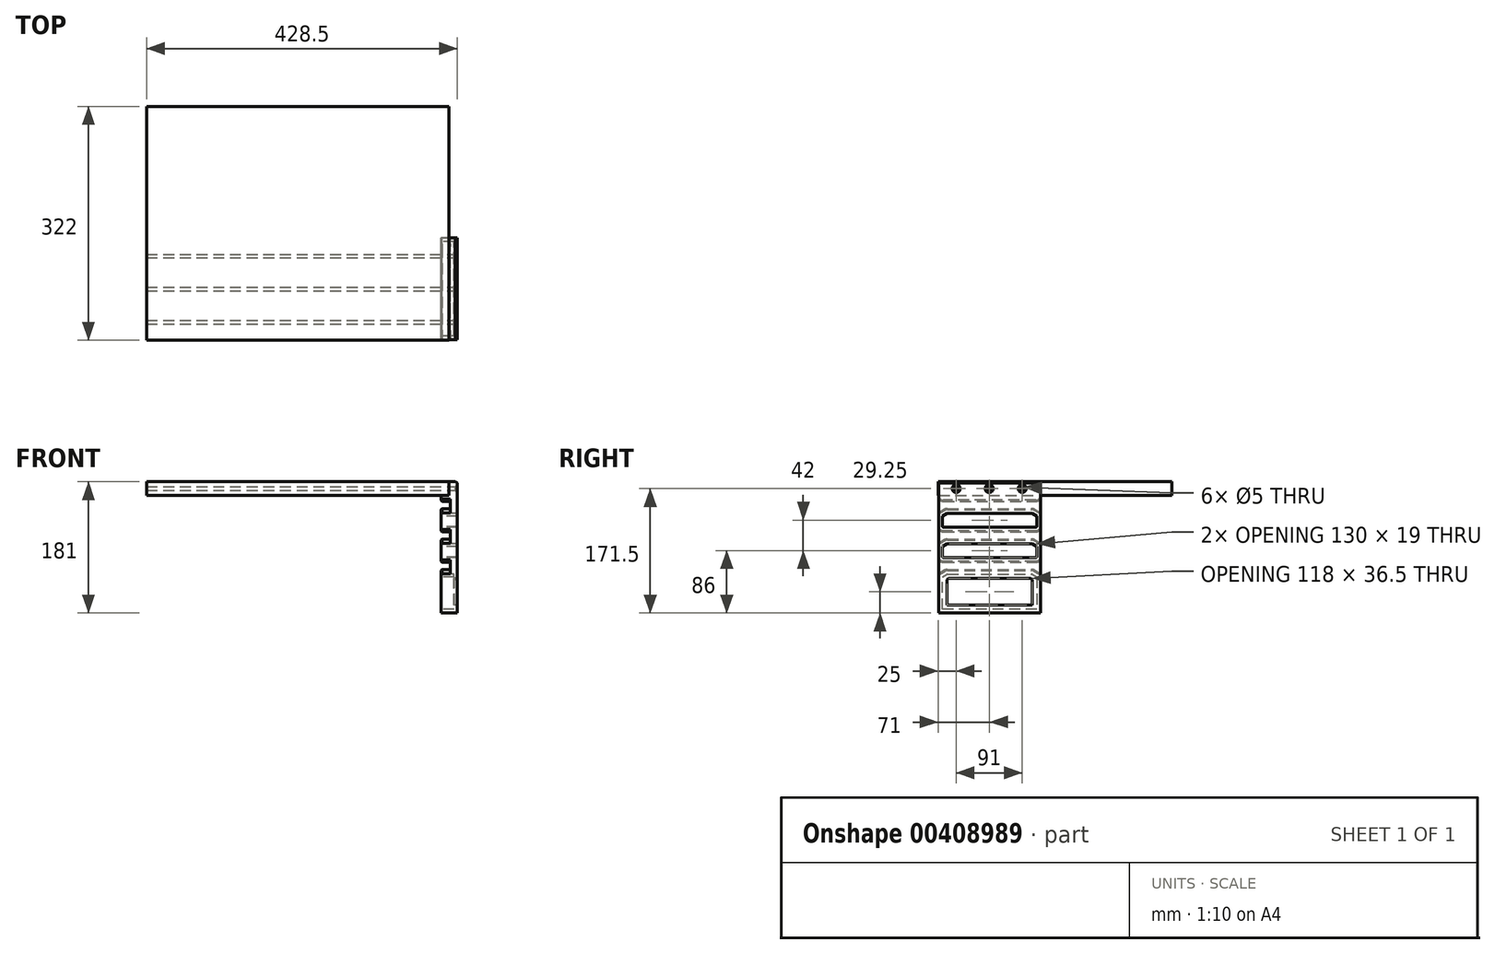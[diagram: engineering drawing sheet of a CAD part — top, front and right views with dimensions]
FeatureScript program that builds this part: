
annotation { "Feature Type Name" : "Feature", "Feature Type Description" : "" }
export const myFeature = defineFeature(function(context is Context, id is Id, definition is map)
    precondition{}
    {
        {
            var Q0;
            Q0=qCreatedBy(makeId("Front.planeOp"),FACE);
            var sketch = newSketch(context, id + "F0", { "sketchPlane" : qUnion([Q0])});
            skLineSegment(sketch, "E0.bottom", {"start": v(0, 0) * mm, "end": v(208.5, 0) * mm});
            skLineSegment(sketch, "E0.top", {"start": v(0, 19) * mm, "end": v(208.5, 19) * mm});
            skLineSegment(sketch, "E0.left", {"start": v(0, 0) * mm, "end": v(0, 19) * mm});
            skLineSegment(sketch, "E0.right", {"start": v(208.5, 0) * mm, "end": v(208.5, 19) * mm});
            skSolve(sketch);
        }
        {
            var Q0;
            Q0=makeQuery(id+"F0.imprint","IMPRINT",FACE,{"disambiguationData":[TD([[makeQuery(id+"F0.imprint","IMPRINT",EDGE,{"derivedFrom":sQuery(id+"F0.wireOp",EDGE,"E0.bottom")}),1.0]])]});
            extrude(context, id + "F1", {"entities" : qUnion([Q0]), "depth" : 161 * mm});
        }
        {
            var Q0;
            Q0=makeQuery(id+"F1.opExtrude","SWEPT_BODY",BODY,{"disambiguationData":[OSD([sQuery(id+"F0.wireOp",EDGE,"E0.bottom"),sQuery(id+"F0.wireOp",EDGE,"E0.top"),sQuery(id+"F0.wireOp",EDGE,"E0.left"),sQuery(id+"F0.wireOp",EDGE,"E0.right")])]});
            var Q1;
            Q1=makeQuery(id+"F1.opExtrude","CAP_FACE",FACE,{"disambiguationData":[OSD([sQuery(id+"F0.wireOp",EDGE,"E0.bottom"),sQuery(id+"F0.wireOp",EDGE,"E0.top"),sQuery(id+"F0.wireOp",EDGE,"E0.left"),sQuery(id+"F0.wireOp",EDGE,"E0.right")])],"isStart":true});
            mirror(context, id + "F2", {"operationType" : NewBodyOperationType.ADD, "entities" : qUnion([Q0]), "mirrorPlane" : qUnion([Q1])});
        }
        {
            var Q0;
            Q0=makeQuery(id+"F1.opExtrude","SWEPT_BODY",BODY,{"disambiguationData":[OSD([sQuery(id+"F0.wireOp",EDGE,"E0.bottom"),sQuery(id+"F0.wireOp",EDGE,"E0.top"),sQuery(id+"F0.wireOp",EDGE,"E0.left"),sQuery(id+"F0.wireOp",EDGE,"E0.right")])]});
            var Q1;
            {var subQ0=makeQuery(id+"F1.opExtrude","SWEPT_FACE",FACE,{"disambiguationData":[OSD([sQuery(id+"F0.wireOp",EDGE,"E0.left")])]});Q1=makeQuery(id+"F2.boolean.opBoolean","MERGE",FACE,{"derivedFrom":[subQ0,makeQuery(id+"F2.opPattern","COPY",FACE,{"derivedFrom":subQ0,"instanceName":"1"})]});}
            mirror(context, id + "F3", {"operationType" : NewBodyOperationType.ADD, "entities" : qUnion([Q0]), "mirrorPlane" : qUnion([Q1])});
        }
        {
            var Q0;
            Q0=qCreatedBy(makeId("Front.planeOp"),FACE);
            var sketch = newSketch(context, id + "F4", { "sketchPlane" : qUnion([Q0])});
            skLineSegment(sketch, "E1", {"start": v(208.5, 19) * mm, "end": v(208.5, 0) * mm});
            skLineSegment(sketch, "E2", {"start": v(208.5, 0) * mm, "end": v(197.5, 0) * mm});
            skLineSegment(sketch, "E3", {"start": v(197.5, 0) * mm, "end": v(197.5, -8) * mm});
            skLineSegment(sketch, "E4", {"start": v(197.5, -8) * mm, "end": v(210, -8) * mm});
            skLineSegment(sketch, "E5", {"start": v(210, -8) * mm, "end": v(210, -18) * mm});
            skLineSegment(sketch, "E6", {"start": v(210, -18) * mm, "end": v(197.5, -18) * mm});
            skLineSegment(sketch, "E7", {"start": v(197.5, -18) * mm, "end": v(197.5, -50) * mm});
            skLineSegment(sketch, "E8", {"start": v(197.5, -50) * mm, "end": v(210, -50) * mm});
            skLineSegment(sketch, "E9", {"start": v(210, -50) * mm, "end": v(210, -60) * mm});
            skLineSegment(sketch, "E10", {"start": v(210, -60) * mm, "end": v(197.5, -60) * mm});
            skLineSegment(sketch, "E11", {"start": v(197.5, -60) * mm, "end": v(197.5, -92) * mm});
            skLineSegment(sketch, "E12", {"start": v(197.5, -162) * mm, "end": v(220, -162) * mm});
            skLineSegment(sketch, "E13", {"start": v(220, -162) * mm, "end": v(220, 19) * mm});
            skLineSegment(sketch, "E14", {"start": v(220, 19) * mm, "end": v(208.5, 19) * mm});
            skLineSegment(sketch, "E15.0", {"start": v(208.5, 0) * mm, "end": v(208.5, 19) * mm});
            skLineSegment(sketch, "E16", {"start": v(197.5, -92) * mm, "end": v(210, -92) * mm});
            skLineSegment(sketch, "E17", {"start": v(210, -92) * mm, "end": v(210, -102) * mm});
            skLineSegment(sketch, "E18", {"start": v(210, -102) * mm, "end": v(197.5, -102) * mm});
            skLineSegment(sketch, "E19.trimOffspring", {"start": v(197.5, -102) * mm, "end": v(197.5, -162) * mm});
            skSolve(sketch);
        }
        {
            var Q0;
            Q0=makeQuery(id+"F4.imprint","IMPRINT",FACE,{"disambiguationData":[TD([[makeQuery(id+"F4.imprint","IMPRINT",EDGE,{"derivedFrom":sQuery(id+"F4.wireOp",EDGE,"E2")}),1.0]])]});
            extrude(context, id + "F5", {"entities" : qUnion([Q0]), "depth" : 160 * mm, "hasSecondDirection" : true, "secondDirectionOppositeDirection" : false, "secondDirectionDepth" : 20 * mm});
        }
        {
            var Q0;
            Q0=makeQuery(id+"F5.opExtrude","CAP_EDGE",EDGE,{"disambiguationData":[OSD([sQuery(id+"F4.wireOp",EDGE,"E6")])],"isStart":false});
            var Q1;
            Q1=makeQuery(id+"F5.opExtrude","CAP_EDGE",EDGE,{"disambiguationData":[OSD([sQuery(id+"F4.wireOp",EDGE,"E10")])],"isStart":false});
            var Q2;
            Q2=makeQuery(id+"F5.opExtrude","CAP_EDGE",EDGE,{"disambiguationData":[OSD([sQuery(id+"F4.wireOp",EDGE,"E18")])],"isStart":false});
            chamfer(context, id + "F6", {"entities" : qUnion([Q0, Q1, Q2]), "chamferType" : ChamferType.OFFSET_ANGLE, "width" : 10 * mm, "oppositeDirection" : true, "angle" : 30 * degree, "tangentPropagation" : true});
        }
        {
            var Q0;
            Q0=makeQuery(id+"F5.opExtrude","CAP_EDGE",EDGE,{"disambiguationData":[OSD([sQuery(id+"F4.wireOp",EDGE,"E6")])],"isStart":true});
            var Q1;
            Q1=makeQuery(id+"F5.opExtrude","CAP_EDGE",EDGE,{"disambiguationData":[OSD([sQuery(id+"F4.wireOp",EDGE,"E10")])],"isStart":true});
            var Q2;
            Q2=makeQuery(id+"F5.opExtrude","CAP_EDGE",EDGE,{"disambiguationData":[OSD([sQuery(id+"F4.wireOp",EDGE,"E18")])],"isStart":true});
            chamfer(context, id + "F7", {"entities" : qUnion([Q0, Q1, Q2]), "chamferType" : ChamferType.OFFSET_ANGLE, "width" : 10 * mm, "oppositeDirection" : false, "angle" : 30 * degree, "tangentPropagation" : true});
        }
        {
            var Q0;
            Q0=makeQuery(id+"F5.opExtrude","CAP_EDGE",EDGE,{"disambiguationData":[OSD([sQuery(id+"F4.wireOp",EDGE,"E4")])],"isStart":true});
            var Q1;
            Q1=makeQuery(id+"F5.opExtrude","CAP_EDGE",EDGE,{"disambiguationData":[OSD([sQuery(id+"F4.wireOp",EDGE,"E8")])],"isStart":true});
            var Q2;
            Q2=makeQuery(id+"F5.opExtrude","CAP_EDGE",EDGE,{"disambiguationData":[OSD([sQuery(id+"F4.wireOp",EDGE,"E16")])],"isStart":true});
            var Q3;
            Q3=makeQuery(id+"F5.opExtrude","CAP_EDGE",EDGE,{"disambiguationData":[OSD([sQuery(id+"F4.wireOp",EDGE,"E16")])],"isStart":false});
            var Q4;
            Q4=makeQuery(id+"F5.opExtrude","CAP_EDGE",EDGE,{"disambiguationData":[OSD([sQuery(id+"F4.wireOp",EDGE,"E8")])],"isStart":false});
            var Q5;
            Q5=makeQuery(id+"F5.opExtrude","CAP_EDGE",EDGE,{"disambiguationData":[OSD([sQuery(id+"F4.wireOp",EDGE,"E4")])],"isStart":false});
            chamfer(context, id + "F8", {"entities" : qUnion([Q0, Q1, Q2, Q3, Q4, Q5]), "width" : 3 * mm, "tangentPropagation" : true});
        }
        {
            var Q0;
            Q0=makeQuery(id+"F5.opExtrude","SWEPT_EDGE",EDGE,{"disambiguationData":[OSD([sQuery(id+"F4.wireOp",EDGE,"E13"),sQuery(id+"F4.wireOp",EDGE,"E14")])]});
            chamfer(context, id + "F9", {"entities" : qUnion([Q0]), "chamferType" : ChamferType.OFFSET_ANGLE, "width" : 3 * mm, "oppositeDirection" : false, "angle" : 30 * degree, "tangentPropagation" : true});
        }
        {
            var Q0;
            {var subQ0=sQuery(id+"F4.wireOp",EDGE,"E18");Q0=makeQuery(id+"F7.opChamfer","BLEND_EDGE",EDGE,{"blendedFrom":[makeQuery(id+"F5.opExtrude","CAP_EDGE",EDGE,{"disambiguationData":[OSD([subQ0])],"isStart":true}),makeQuery(id+"F5.opExtrude","SWEPT_FACE",FACE,{"disambiguationData":[OSD([subQ0])]})],"blendedInto":[makeQuery(id+"F5.opExtrude","SWEPT_FACE",FACE,{"disambiguationData":[OSD([subQ0])]})]});}
            var Q1;
            {var subQ0=sQuery(id+"F4.wireOp",EDGE,"E18");Q1=makeQuery(id+"F6.opChamfer","BLEND_EDGE",EDGE,{"blendedFrom":[makeQuery(id+"F5.opExtrude","CAP_EDGE",EDGE,{"disambiguationData":[OSD([subQ0])],"isStart":false}),makeQuery(id+"F5.opExtrude","SWEPT_FACE",FACE,{"disambiguationData":[OSD([subQ0])]})],"blendedInto":[makeQuery(id+"F5.opExtrude","SWEPT_FACE",FACE,{"disambiguationData":[OSD([subQ0])]})]});}
            var Q2;
            {var subQ0=sQuery(id+"F4.wireOp",EDGE,"E10");Q2=makeQuery(id+"F6.opChamfer","BLEND_EDGE",EDGE,{"blendedFrom":[makeQuery(id+"F5.opExtrude","CAP_EDGE",EDGE,{"disambiguationData":[OSD([subQ0])],"isStart":false}),makeQuery(id+"F5.opExtrude","SWEPT_FACE",FACE,{"disambiguationData":[OSD([subQ0])]})],"blendedInto":[makeQuery(id+"F5.opExtrude","SWEPT_FACE",FACE,{"disambiguationData":[OSD([subQ0])]})]});}
            var Q3;
            {var subQ0=sQuery(id+"F4.wireOp",EDGE,"E6");Q3=makeQuery(id+"F6.opChamfer","BLEND_EDGE",EDGE,{"blendedFrom":[makeQuery(id+"F5.opExtrude","CAP_EDGE",EDGE,{"disambiguationData":[OSD([subQ0])],"isStart":false}),makeQuery(id+"F5.opExtrude","SWEPT_FACE",FACE,{"disambiguationData":[OSD([subQ0])]})],"blendedInto":[makeQuery(id+"F5.opExtrude","SWEPT_FACE",FACE,{"disambiguationData":[OSD([subQ0])]})]});}
            var Q4;
            {var subQ0=sQuery(id+"F4.wireOp",EDGE,"E10");Q4=makeQuery(id+"F7.opChamfer","BLEND_EDGE",EDGE,{"blendedFrom":[makeQuery(id+"F5.opExtrude","CAP_EDGE",EDGE,{"disambiguationData":[OSD([subQ0])],"isStart":true}),makeQuery(id+"F5.opExtrude","SWEPT_FACE",FACE,{"disambiguationData":[OSD([subQ0])]})],"blendedInto":[makeQuery(id+"F5.opExtrude","SWEPT_FACE",FACE,{"disambiguationData":[OSD([subQ0])]})]});}
            var Q5;
            {var subQ0=sQuery(id+"F4.wireOp",EDGE,"E6");Q5=makeQuery(id+"F7.opChamfer","BLEND_EDGE",EDGE,{"blendedFrom":[makeQuery(id+"F5.opExtrude","CAP_EDGE",EDGE,{"disambiguationData":[OSD([subQ0])],"isStart":true}),makeQuery(id+"F5.opExtrude","SWEPT_FACE",FACE,{"disambiguationData":[OSD([subQ0])]})],"blendedInto":[makeQuery(id+"F5.opExtrude","SWEPT_FACE",FACE,{"disambiguationData":[OSD([subQ0])]})]});}
            var Q6;
            {var subQ0=sQuery(id+"F4.wireOp",EDGE,"E4");Q6=makeQuery(id+"F8.opChamfer","BLEND_EDGE",EDGE,{"blendedFrom":[makeQuery(id+"F5.opExtrude","CAP_EDGE",EDGE,{"disambiguationData":[OSD([subQ0])],"isStart":true}),makeQuery(id+"F5.opExtrude","SWEPT_FACE",FACE,{"disambiguationData":[OSD([subQ0])]})],"blendedInto":[makeQuery(id+"F5.opExtrude","SWEPT_FACE",FACE,{"disambiguationData":[OSD([subQ0])]})]});}
            var Q7;
            {var subQ0=sQuery(id+"F4.wireOp",EDGE,"E4");Q7=makeQuery(id+"F8.opChamfer","BLEND_EDGE",EDGE,{"blendedFrom":[makeQuery(id+"F5.opExtrude","CAP_EDGE",EDGE,{"disambiguationData":[OSD([subQ0])],"isStart":false}),makeQuery(id+"F5.opExtrude","SWEPT_FACE",FACE,{"disambiguationData":[OSD([subQ0])]})],"blendedInto":[makeQuery(id+"F5.opExtrude","SWEPT_FACE",FACE,{"disambiguationData":[OSD([subQ0])]})]});}
            var Q8;
            {var subQ0=sQuery(id+"F4.wireOp",EDGE,"E8");Q8=makeQuery(id+"F8.opChamfer","BLEND_EDGE",EDGE,{"blendedFrom":[makeQuery(id+"F5.opExtrude","CAP_EDGE",EDGE,{"disambiguationData":[OSD([subQ0])],"isStart":true}),makeQuery(id+"F5.opExtrude","SWEPT_FACE",FACE,{"disambiguationData":[OSD([subQ0])]})],"blendedInto":[makeQuery(id+"F5.opExtrude","SWEPT_FACE",FACE,{"disambiguationData":[OSD([subQ0])]})]});}
            var Q9;
            {var subQ0=sQuery(id+"F4.wireOp",EDGE,"E16");Q9=makeQuery(id+"F8.opChamfer","BLEND_EDGE",EDGE,{"blendedFrom":[makeQuery(id+"F5.opExtrude","CAP_EDGE",EDGE,{"disambiguationData":[OSD([subQ0])],"isStart":true}),makeQuery(id+"F5.opExtrude","SWEPT_FACE",FACE,{"disambiguationData":[OSD([subQ0])]})],"blendedInto":[makeQuery(id+"F5.opExtrude","SWEPT_FACE",FACE,{"disambiguationData":[OSD([subQ0])]})]});}
            var Q10;
            {var subQ0=sQuery(id+"F4.wireOp",EDGE,"E16");Q10=makeQuery(id+"F8.opChamfer","BLEND_EDGE",EDGE,{"blendedFrom":[makeQuery(id+"F5.opExtrude","CAP_EDGE",EDGE,{"disambiguationData":[OSD([subQ0])],"isStart":false}),makeQuery(id+"F5.opExtrude","SWEPT_FACE",FACE,{"disambiguationData":[OSD([subQ0])]})],"blendedInto":[makeQuery(id+"F5.opExtrude","SWEPT_FACE",FACE,{"disambiguationData":[OSD([subQ0])]})]});}
            var Q11;
            {var subQ0=sQuery(id+"F4.wireOp",EDGE,"E8");Q11=makeQuery(id+"F8.opChamfer","BLEND_EDGE",EDGE,{"blendedFrom":[makeQuery(id+"F5.opExtrude","CAP_EDGE",EDGE,{"disambiguationData":[OSD([subQ0])],"isStart":false}),makeQuery(id+"F5.opExtrude","SWEPT_FACE",FACE,{"disambiguationData":[OSD([subQ0])]})],"blendedInto":[makeQuery(id+"F5.opExtrude","SWEPT_FACE",FACE,{"disambiguationData":[OSD([subQ0])]})]});}
            fillet(context, id + "F10", {"entities" : qUnion([Q0, Q1, Q2, Q3, Q4, Q5, Q6, Q7, Q8, Q9, Q10, Q11]), "radius" : 8 * mm, "tangentPropagation" : true, "allowEdgeOverflow" : false});
        }
        {
            var Q0;
            Q0=makeQuery(id+"F7.opChamfer","BLEND_EDGE",EDGE,{"blendedFrom":[makeQuery(id+"F5.opExtrude","CAP_EDGE",EDGE,{"disambiguationData":[OSD([sQuery(id+"F4.wireOp",EDGE,"E6")])],"isStart":true}),makeQuery(id+"F5.opExtrude","SWEPT_FACE",FACE,{"disambiguationData":[OSD([sQuery(id+"F4.wireOp",EDGE,"E7")])]})],"blendedInto":[makeQuery(id+"F5.opExtrude","SWEPT_FACE",FACE,{"disambiguationData":[OSD([sQuery(id+"F4.wireOp",EDGE,"E7")])]})]});
            var Q1;
            Q1=makeQuery(id+"F5.opExtrude","SWEPT_EDGE",EDGE,{"disambiguationData":[OSD([sQuery(id+"F4.wireOp",EDGE,"E3"),sQuery(id+"F4.wireOp",EDGE,"E4")])]});
            var Q2;
            Q2=makeQuery(id+"F5.opExtrude","SWEPT_EDGE",EDGE,{"disambiguationData":[OSD([sQuery(id+"F4.wireOp",EDGE,"E7"),sQuery(id+"F4.wireOp",EDGE,"E8")])]});
            var Q3;
            Q3=makeQuery(id+"F5.opExtrude","SWEPT_EDGE",EDGE,{"disambiguationData":[OSD([sQuery(id+"F4.wireOp",EDGE,"E10"),sQuery(id+"F4.wireOp",EDGE,"E11")])]});
            var Q4;
            Q4=makeQuery(id+"F5.opExtrude","SWEPT_EDGE",EDGE,{"disambiguationData":[OSD([sQuery(id+"F4.wireOp",EDGE,"E18"),sQuery(id+"F4.wireOp",EDGE,"E19.trimOffspring")])]});
            var Q5;
            Q5=makeQuery(id+"F5.opExtrude","SWEPT_EDGE",EDGE,{"disambiguationData":[OSD([sQuery(id+"F4.wireOp",EDGE,"E11"),sQuery(id+"F4.wireOp",EDGE,"E16")])]});
            chamfer(context, id + "F11", {"entities" : qUnion([Q0, Q1, Q2, Q3, Q4, Q5]), "width" : 1.5 * mm, "tangentPropagation" : true});
        }
        {
            var Q0;
            Q0=makeQuery(id+"F5.opExtrude","SWEPT_FACE",FACE,{"disambiguationData":[OSD([sQuery(id+"F4.wireOp",EDGE,"E7")])]});
            var sketch = newSketch(context, id + "F12", { "sketchPlane" : qUnion([Q0])});
            skLineSegment(sketch, "E20.0", {"start": v(26.31, -43.5) * mm, "end": v(153.69, -43.5) * mm});
            skArc(sketch, "E20.1", {"start": v(148.6, -24.7) * mm, "mid": v(148.24, -24.55) * mm, "end": v(147.86, -24.5) * mm});
            skLineSegment(sketch, "E20.2", {"start": v(155, -28.4) * mm, "end": v(148.6, -24.7) * mm});
            skLineSegment(sketch, "E20.3", {"start": v(155, -42.8) * mm, "end": v(155, -28.4) * mm});
            skLineSegment(sketch, "E20.4", {"start": v(154.75, -43.06) * mm, "end": v(155, -42.8) * mm});
            skLineSegment(sketch, "E20.5", {"start": v(147.86, -24.5) * mm, "end": v(32.14, -24.5) * mm});
            skArc(sketch, "E20.6", {"start": v(153.69, -43.5) * mm, "mid": v(154.26, -43.39) * mm, "end": v(154.75, -43.06) * mm});
            skArc(sketch, "E20.7", {"start": v(32.14, -24.5) * mm, "mid": v(31.76, -24.55) * mm, "end": v(31.4, -24.7) * mm});
            skLineSegment(sketch, "E20.8", {"start": v(31.4, -24.7) * mm, "end": v(25, -28.4) * mm});
            skLineSegment(sketch, "E20.9", {"start": v(25, -28.4) * mm, "end": v(25, -42.8) * mm});
            skLineSegment(sketch, "E20.10", {"start": v(25, -42.8) * mm, "end": v(25.25, -43.06) * mm});
            skArc(sketch, "E20.11", {"start": v(25.25, -43.06) * mm, "mid": v(25.74, -43.39) * mm, "end": v(26.31, -43.5) * mm});
            skLineSegment(sketch, "E21.0", {"start": v(26.31, -85.5) * mm, "end": v(153.69, -85.5) * mm});
            skArc(sketch, "E21.1", {"start": v(148.6, -66.7) * mm, "mid": v(148.24, -66.55) * mm, "end": v(147.86, -66.5) * mm});
            skLineSegment(sketch, "E21.2", {"start": v(155, -70.4) * mm, "end": v(148.6, -66.7) * mm});
            skLineSegment(sketch, "E21.3", {"start": v(155, -84.8) * mm, "end": v(155, -70.4) * mm});
            skLineSegment(sketch, "E21.4", {"start": v(154.75, -85.06) * mm, "end": v(155, -84.8) * mm});
            skLineSegment(sketch, "E21.5", {"start": v(147.86, -66.5) * mm, "end": v(32.14, -66.5) * mm});
            skArc(sketch, "E21.6", {"start": v(153.69, -85.5) * mm, "mid": v(154.26, -85.39) * mm, "end": v(154.75, -85.06) * mm});
            skArc(sketch, "E21.7", {"start": v(32.14, -66.5) * mm, "mid": v(31.76, -66.55) * mm, "end": v(31.4, -66.7) * mm});
            skLineSegment(sketch, "E21.8", {"start": v(31.4, -66.7) * mm, "end": v(25, -70.4) * mm});
            skLineSegment(sketch, "E21.9", {"start": v(25, -70.4) * mm, "end": v(25, -84.8) * mm});
            skLineSegment(sketch, "E21.10", {"start": v(25, -84.8) * mm, "end": v(25.25, -85.06) * mm});
            skArc(sketch, "E21.11", {"start": v(25.25, -85.06) * mm, "mid": v(25.74, -85.39) * mm, "end": v(26.31, -85.5) * mm});
            skLineSegment(sketch, "E22.0", {"start": v(25, -157) * mm, "end": v(155, -157) * mm});
            skLineSegment(sketch, "E22.1", {"start": v(25, -112.4) * mm, "end": v(25, -157) * mm});
            skLineSegment(sketch, "E22.2", {"start": v(155, -157) * mm, "end": v(155, -112.4) * mm});
            skLineSegment(sketch, "E22.3", {"start": v(31.4, -108.7) * mm, "end": v(25, -112.4) * mm});
            skLineSegment(sketch, "E22.4", {"start": v(155, -112.4) * mm, "end": v(148.6, -108.7) * mm});
            skArc(sketch, "E22.5", {"start": v(148.6, -108.7) * mm, "mid": v(148.24, -108.55) * mm, "end": v(147.86, -108.5) * mm});
            skLineSegment(sketch, "E22.6", {"start": v(147.86, -108.5) * mm, "end": v(32.14, -108.5) * mm});
            skArc(sketch, "E22.7", {"start": v(32.14, -108.5) * mm, "mid": v(31.76, -108.55) * mm, "end": v(31.4, -108.7) * mm});
            skSolve(sketch);
        }
        {
            var Q0;
            Q0=makeQuery(id+"F12.imprint","IMPRINT",FACE,{"disambiguationData":[TD([[makeQuery(id+"F12.imprint","IMPRINT",EDGE,{"derivedFrom":sQuery(id+"F12.wireOp",EDGE,"E20.0")}),1.0]])]});
            var Q1;
            Q1=makeQuery(id+"F12.imprint","IMPRINT",FACE,{"disambiguationData":[TD([[makeQuery(id+"F12.imprint","IMPRINT",EDGE,{"derivedFrom":sQuery(id+"F12.wireOp",EDGE,"E21.0")}),1.0]])]});
            extrude(context, id + "F13", {"entities" : qUnion([Q0, Q1]), "operationType" : NewBodyOperationType.REMOVE, "endBound" : BoundingType.UP_TO_NEXT, "oppositeDirection" : true, "depth" : 18 * mm});
        }
        {
            var Q0;
            Q0=makeQuery(id+"F5.opExtrude","SWEPT_FACE",FACE,{"disambiguationData":[OSD([sQuery(id+"F4.wireOp",EDGE,"E13")])]});
            var sketch = newSketch(context, id + "F14", { "sketchPlane" : qUnion([Q0])});
            skLineSegment(sketch, "E23.0", {"start": v(-161, 0) * mm, "end": v(161, 0) * mm});
            skLineSegment(sketch, "E24.0", {"start": v(-161, 9.5) * mm, "end": v(161, 9.5) * mm, "construction": true});
            skPoint(sketch, "E25", {"position": v(-45, 9.5) * mm});
            skPoint(sketch, "E26", {"position": v(-136, 9.5) * mm});
            skPoint(sketch, "E27", {"position": v(-90.5, 9.5) * mm});
            skSolve(sketch);
        }
        {
            var Q0;
            Q0=sQuery(id+"F14.wireOp",VERTEX,"E26");
            var Q1;
            Q1=sQuery(id+"F14.wireOp",VERTEX,"E27");
            var Q2;
            Q2=sQuery(id+"F14.wireOp",VERTEX,"E25");
            var Q3;
            Q3=makeQuery(id+"F1.opExtrude","SWEPT_BODY",BODY,{"disambiguationData":[OSD([sQuery(id+"F0.wireOp",EDGE,"E0.bottom"),sQuery(id+"F0.wireOp",EDGE,"E0.top"),sQuery(id+"F0.wireOp",EDGE,"E0.left"),sQuery(id+"F0.wireOp",EDGE,"E0.right")])]});
            var Q4;
            Q4=makeQuery(id+"F5.opExtrude","SWEPT_BODY",BODY,{"disambiguationData":[OSD([sQuery(id+"F4.wireOp",EDGE,"E2"),sQuery(id+"F4.wireOp",EDGE,"E3"),sQuery(id+"F4.wireOp",EDGE,"E4"),sQuery(id+"F4.wireOp",EDGE,"E5"),sQuery(id+"F4.wireOp",EDGE,"E6"),sQuery(id+"F4.wireOp",EDGE,"E7"),sQuery(id+"F4.wireOp",EDGE,"E8"),sQuery(id+"F4.wireOp",EDGE,"E9"),sQuery(id+"F4.wireOp",EDGE,"E10"),sQuery(id+"F4.wireOp",EDGE,"E11"),sQuery(id+"F4.wireOp",EDGE,"E12"),sQuery(id+"F4.wireOp",EDGE,"E13"),sQuery(id+"F4.wireOp",EDGE,"E14"),sQuery(id+"F4.wireOp",EDGE,"E15.0"),sQuery(id+"F4.wireOp",EDGE,"E16"),sQuery(id+"F4.wireOp",EDGE,"E17"),sQuery(id+"F4.wireOp",EDGE,"E18"),sQuery(id+"F4.wireOp",EDGE,"E19.trimOffspring")])]});
            hole(context, id + "F15", {"style" : HoleStyle.C_SINK, "endStyle" : HoleEndStyle.THROUGH, "holeDiameter" : 5 * mm, "cSinkDiameter" : 11 * mm, "cSinkAngle" : 90 * degree, "isTappedThrough" : true, "tappedDepth" : 12 * mm, "tapClearance" : 3, "startFromSketch" : true, "locations" : qUnion([Q0, Q1, Q2]), "scope" : qUnion([Q3, Q4])});
        }
        {
            var Q0;
            Q0=makeQuery(id+"F12.imprint","IMPRINT",FACE,{"disambiguationData":[TD([[makeQuery(id+"F12.imprint","IMPRINT",EDGE,{"derivedFrom":sQuery(id+"F12.wireOp",EDGE,"E22.0")}),1.0]])]});
            extrude(context, id + "F16", {"entities" : qUnion([Q0]), "operationType" : NewBodyOperationType.REMOVE, "oppositeDirection" : true, "depth" : 18 * mm});
        }
        {
            var Q0;
            Q0=makeQuery(id+"F12.imprint","IMPRINT",FACE,{"disambiguationData":[TD([[makeQuery(id+"F12.imprint","IMPRINT",EDGE,{"derivedFrom":sQuery(id+"F12.wireOp",EDGE,"E22.0")}),1.0]])]});
            var sketch = newSketch(context, id + "F17", { "sketchPlane" : qUnion([Q0])});
            skLineSegment(sketch, "E28.0", {"start": v(149, -115.86) * mm, "end": v(146.65, -114.5) * mm});
            skLineSegment(sketch, "E28.1", {"start": v(33.35, -114.5) * mm, "end": v(31, -115.86) * mm});
            skLineSegment(sketch, "E28.2", {"start": v(31, -115.86) * mm, "end": v(31, -151) * mm});
            skLineSegment(sketch, "E28.3", {"start": v(146.65, -114.5) * mm, "end": v(33.35, -114.5) * mm});
            skLineSegment(sketch, "E28.4", {"start": v(31, -151) * mm, "end": v(149, -151) * mm});
            skLineSegment(sketch, "E28.5", {"start": v(149, -151) * mm, "end": v(149, -115.86) * mm});
            skSolve(sketch);
        }
        {
            var Q0;
            Q0=makeQuery(id+"F17.imprint","IMPRINT",FACE,{"disambiguationData":[TD([[makeQuery(id+"F17.imprint","IMPRINT",EDGE,{"derivedFrom":sQuery(id+"F17.wireOp",EDGE,"E28.0")}),1.0]])]});
            extrude(context, id + "F18", {"entities" : qUnion([Q0]), "operationType" : NewBodyOperationType.REMOVE, "endBound" : BoundingType.THROUGH_ALL, "oppositeDirection" : true, "depth" : 25 * mm});
        }
    });
